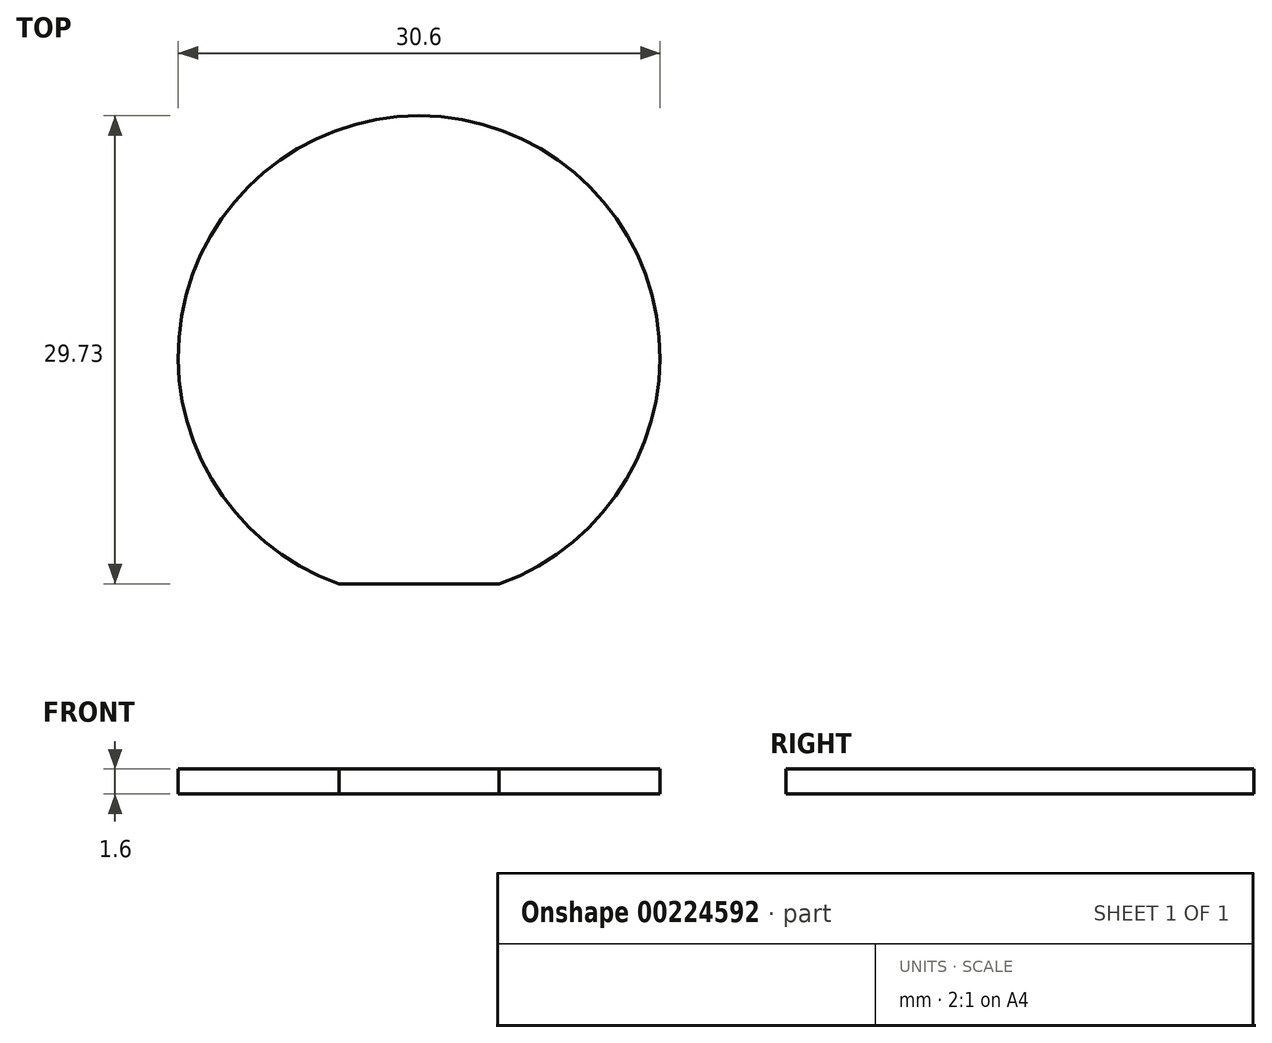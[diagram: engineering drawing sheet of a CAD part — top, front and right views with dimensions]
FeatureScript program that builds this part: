
annotation { "Feature Type Name" : "Feature", "Feature Type Description" : "" }
export const myFeature = defineFeature(function(context is Context, id is Id, definition is map)
    precondition{}
    {
        {
            var Q0;
            Q0=qCreatedBy(makeId("Top.planeOp"),FACE);
            var sketch = newSketch(context, id + "F0", { "sketchPlane" : qUnion([Q0])});
            skLineSegment(sketch, "E0", {"start": v(0, -8.76) * mm, "end": v(5.08, -8.76) * mm, "construction": true});
            skLineSegment(sketch, "E1", {"start": v(5.08, -8.76) * mm, "end": v(5.08, -14.43) * mm, "construction": true});
            skLineSegment(sketch, "E2", {"start": v(5.08, -14.43) * mm, "end": v(-5.08, -14.43) * mm});
            skArc(sketch, "E3", {"start": v(5.08, -14.43) * mm, "mid": v(0, 15.3) * mm, "end": v(-5.08, -14.43) * mm});
            skSolve(sketch);
        }
        {
            var Q0;
            Q0 = qSketchRegion(id + "F0", true);
            extrude(context, id + "F1", {"entities" : qUnion([Q0]), "depth" : 1.6 * mm, "offsetDistance" : 25 * mm});
        }
    });
